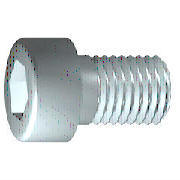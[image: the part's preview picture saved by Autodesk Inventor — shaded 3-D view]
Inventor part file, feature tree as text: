
AUTODESK INVENTOR PART (.ipt)
format: ipt  version: 2019 (Build 230136000, 136)  size: 194,048 bytes
history: native  units: mm (DEFAULTED — no unit token found)
features: sketch x2, extrude x1, plane x1, fillet x1
ambient origin geometry x7: Origin, YZ Plane, XY Plane, X Axis, Y Axis, Z Axis, Center Point
bodies: Solid1 (feature_tree), Body (feature_tree)
feature tree (5):
  extrude  "Slot"  Depth=4.0mm
  plane  "Work Plane1"
  fillet  "Fillet2"  Radius=4.0mm
  sketch  "Sketch1"  dims[d1=13.9mm d2=0.429515mm d3=4.0mm]
  sketch  "Sketch2"  dims[d4=2.0mm d5=60.0deg d6=4.0mm d7=4.0mm d8=3.464102mm d9=7.0mm d10=90.0deg d11=10.0mm d12=0.0mm d13=13.9mm d14=0.0mm d15=0.429415mm d16=0.429415mm d17=0.4mm d19=0.0mm d26=16.0mm d27=45.0deg d28=0.0mm d29=0.0mm d30=0.1mm]
